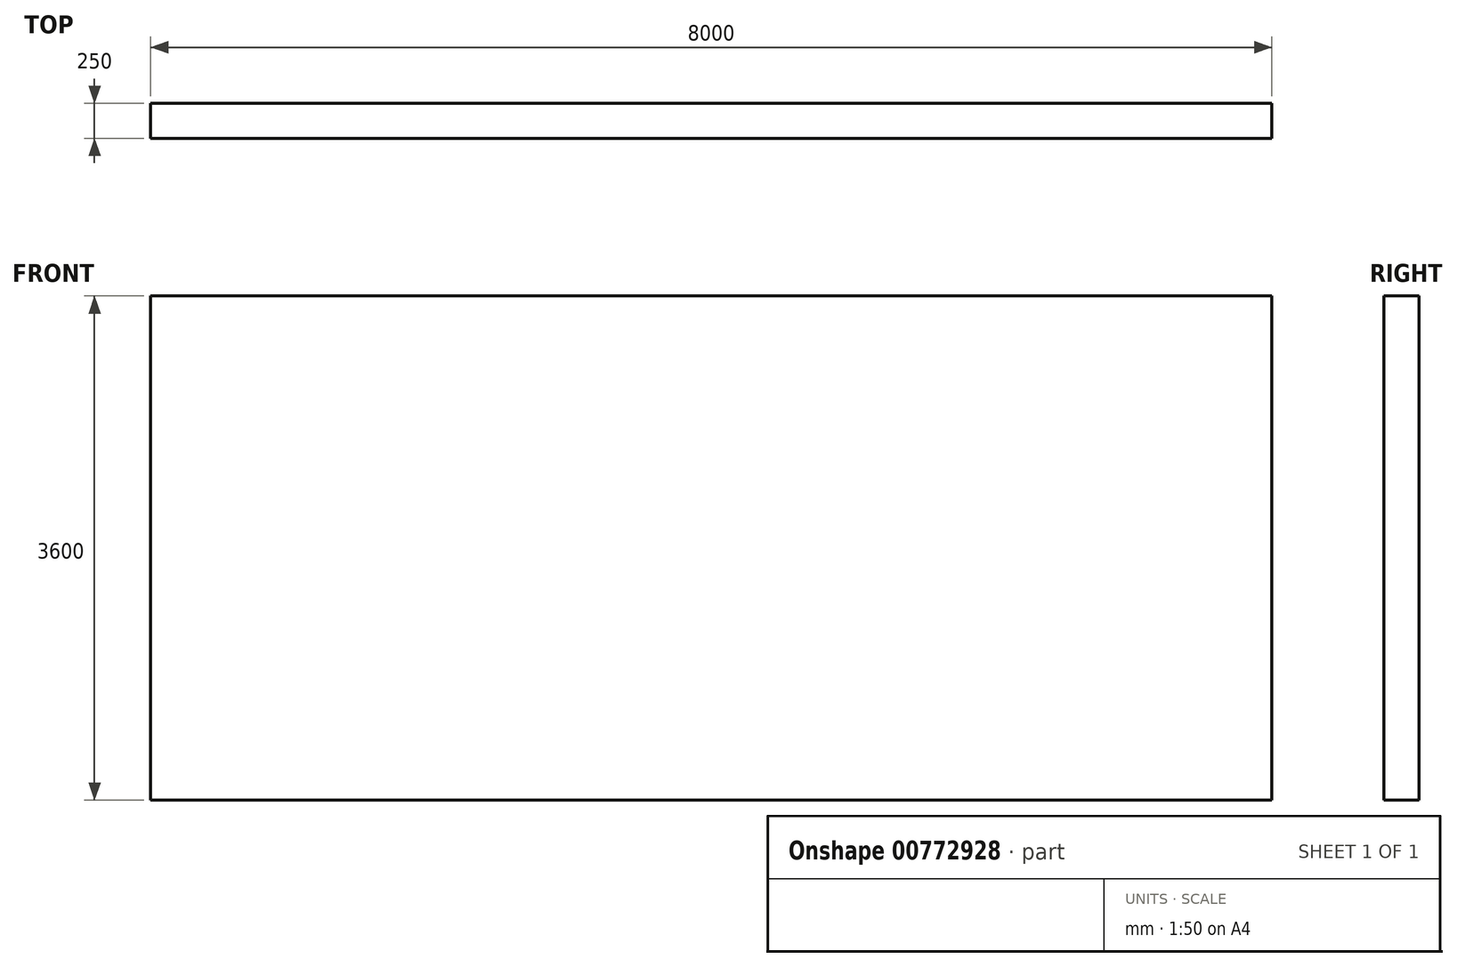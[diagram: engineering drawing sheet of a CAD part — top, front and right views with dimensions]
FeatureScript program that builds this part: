
annotation { "Feature Type Name" : "Feature", "Feature Type Description" : "" }
export const myFeature = defineFeature(function(context is Context, id is Id, definition is map)
    precondition{}
    {
        {
            var Q0;
            Q0=qCreatedBy(makeId("Front.planeOp"),FACE);
            var sketch = newSketch(context, id + "F0", { "sketchPlane" : qUnion([Q0])});
            skLineSegment(sketch, "E0.bottom", {"start": v(-3998.31, 928.9) * mm, "end": v(4001.69, 928.9) * mm});
            skLineSegment(sketch, "E0.top", {"start": v(-3998.31, -2671.1) * mm, "end": v(4001.69, -2671.1) * mm});
            skLineSegment(sketch, "E0.left", {"start": v(-3998.31, 928.9) * mm, "end": v(-3998.31, -2671.1) * mm});
            skLineSegment(sketch, "E0.right", {"start": v(4001.69, 928.9) * mm, "end": v(4001.69, -2671.1) * mm});
            skSolve(sketch);
        }
        {
            var Q0;
            Q0 = qSketchRegion(id + "F0", true);
            extrude(context, id + "F1", {"entities" : qUnion([Q0]), "depth" : 250 * mm, "offsetDistance" : 25 * mm});
        }
    });
